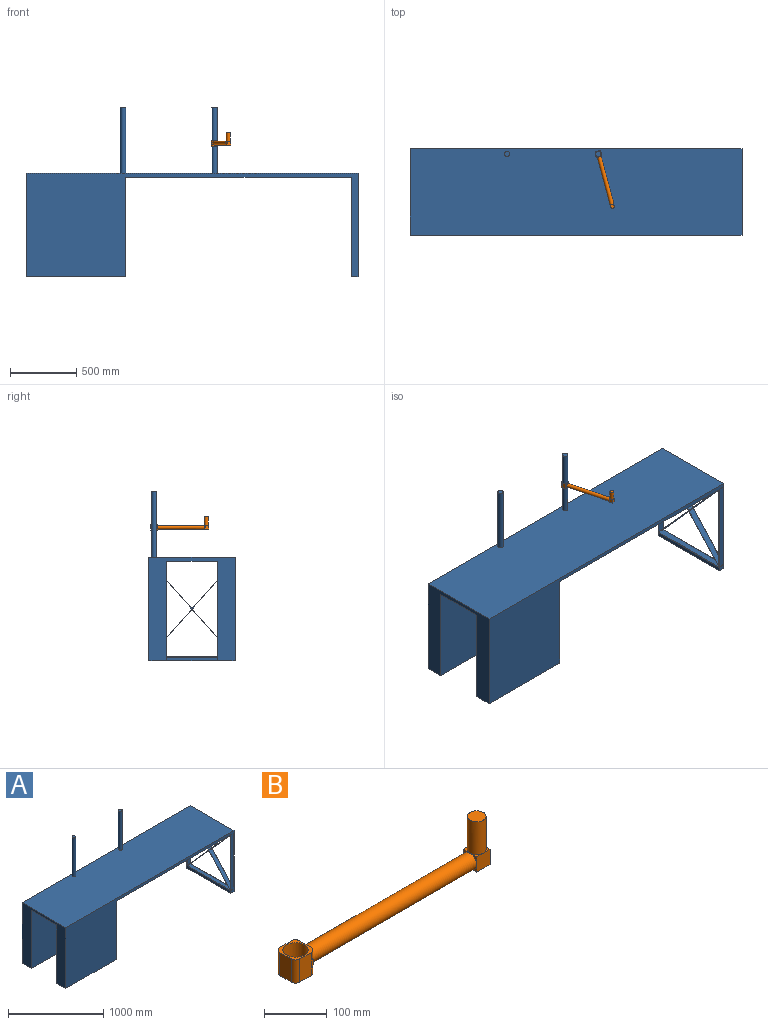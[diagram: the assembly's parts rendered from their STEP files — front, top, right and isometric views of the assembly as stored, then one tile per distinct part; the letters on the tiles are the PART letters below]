
ASSEMBLY  parts=2 mates=1
PART A: 37 faces, bbox 2500x650x1280 mm
  f0: plane 712.61x50mm, normal (0,1,0), area 35630.5mm2, adj f11,f19,f30,f31
  f1: plane 712.61x50mm, normal (0,-1,0), area 35630.5mm2, adj f11,f19,f34,f35
  f2: plane 2500x650mm, normal (0,0,-1), area 1421998.4mm2, adj f8,f9,f10,f11,f13,f14,f16,f17
  f3: plane 638.89x48.8mm, normal (0,0,1), area 31177.8mm2, adj f4,f5,f32,f33
  f4: cylinder r=0.6mm len=639.97mm, axis (0,1,0), area 602.5mm2, adj f3,f19,f32,f33
  f5: cylinder r=0.6mm len=639.97mm, axis (0,-1,0), area 602.5mm2, adj f3,f11,f32,f33
  f6: plane 50x1.1mm, normal (0,1,0), area 25.2mm2, adj f11,f19,f21,f22,f23,f24
  f7: plane 50x1.1mm, normal (0,-1,0), area 25.2mm2, adj f11,f19,f21,f22,f23,f24
  f8: plane 2500x780mm, normal (0,1,0), area 675000mm2, adj f2,f9,f11,f12,f16,f18,f19,f20
  f9: plane 780x650mm, normal (-1,0,0), area 222000mm2, adj f2,f8,f10,f12,f13,f15,f17,f18
  f10: plane 2500x780mm, normal (0,-1,0), area 675000mm2, adj f2,f9,f11,f12,f14,f15,f19,f20
  f11: plane 780x650mm, normal (1,0,0), area 50244.1mm2, adj f0,f1,f2,f5,f6,f7,f8,f10
  f12: plane 2500x650mm, normal (0,0,1), area 1622486.7mm2, adj f8,f9,f10,f11,f25,f27
  f13: plane 750x750mm, normal (0,1,0), area 562500mm2, adj f2,f9,f14,f15
  f14: plane 750x135mm, normal (1,0,0), area 101250mm2, adj f2,f10,f13,f15
  f15: plane 750x135mm, normal (0,0,-1), area 101250mm2, adj f9,f10,f13,f14
  f16: plane 750x135mm, normal (1,0,0), area 101250mm2, adj f2,f8,f17,f18
  f17: plane 750x750mm, normal (0,-1,0), area 562500mm2, adj f2,f9,f16,f18
  f18: plane 750x135mm, normal (0,0,-1), area 101250mm2, adj f8,f9,f16,f17
  f19: plane 750x650mm, normal (-1,0,0), area 30744.1mm2, adj f0,f1,f2,f4,f6,f7,f8,f10
  f20: plane 650x50mm, normal (0,0,-1), area 32500mm2, adj f8,f10,f11,f19
  f21: plane 644x50mm, normal (0,0,1), area 32200mm2, adj f6,f7,f11,f19
  f22: plane 644x48.8mm, normal (0,0,-1), area 31427.2mm2, adj f6,f7,f23,f24
  f23: cylinder r=0.6mm len=644mm, axis (0,1,0), area 607mm2, adj f6,f7,f11,f22
  f24: cylinder r=0.6mm len=644mm, axis (0,-1,0), area 607mm2, adj f6,f7,f19,f22
  f25: cylinder r=20mm len=500mm, axis (0,0,-1), area 62831.9mm2, adj f12,f26
  f26: plane 40x40mm, normal (0,0,1), area 1256.6mm2, adj f25
  f27: cylinder r=20mm len=500mm, axis (0,0,-1), area 62831.9mm2, adj f12,f28
  f28: plane 40x40mm, normal (0,0,1), area 1256.6mm2, adj f27
  f29: plane 356.31x319.98mm, normal (0,0.74,0.67), area 23944.9mm2, adj f2,f11,f19,f36
  f30: plane 356.31x319.98mm, normal (0,-0.74,-0.67), area 23944.9mm2, adj f0,f11,f19,f31
  f31: plane 356.31x319.98mm, normal (0,-0.74,0.67), area 23944.9mm2, adj f0,f11,f19,f30
  f32: plane 356.31x319.98mm, normal (0,0.74,-0.67), area 23904.8mm2, adj f3,f4,f5,f11,f19,f33
  f33: plane 356.31x319.98mm, normal (0,-0.74,-0.67), area 23904.8mm2, adj f3,f4,f5,f11,f19,f32
  f34: plane 356.31x319.98mm, normal (0,0.74,0.67), area 23944.9mm2, adj f1,f11,f19,f35
  f35: plane 356.31x319.98mm, normal (0,0.74,-0.67), area 23944.9mm2, adj f1,f11,f19,f34
  f36: plane 356.31x319.98mm, normal (0,-0.74,0.67), area 23944.9mm2, adj f2,f11,f19,f29
PART B: 31 faces, bbox 445x45x101.5 mm
  f0: plane 25.69x14.75mm, normal (1,0,0), area 247.1mm2, adj f4,f19,f23,f26
  f1: plane 15x15mm, normal (0,0,1), area 48.3mm2, adj f11,f13,f14
  f2: plane 15x15mm, normal (0,0,1), area 48.3mm2, adj f6,f11,f14
  f3: plane 15x15mm, normal (0,0,1), area 48.3mm2, adj f7,f9,f14
  f4: cylinder r=15mm len=370mm, axis (-1,0,0), area 34871.7mm2, adj f0,f5,f6,f7,f8,f21,f24,f27
  f5: plane 15x15mm, normal (-1,0,0), area 48.3mm2, adj f4,f10,f11
  f6: plane 15x15mm, normal (-1,0,0), area 48.3mm2, adj f2,f4,f11
  f7: plane 15x15mm, normal (-1,0,0), area 48.3mm2, adj f3,f4,f9
  f8: plane 15x15mm, normal (-1,0,0), area 48.3mm2, adj f4,f9,f10
  f9: plane 30x30mm, normal (0,-1,0), area 900mm2, adj f3,f7,f8,f10,f12,f13
  f10: plane 30x30mm, normal (0,0,-1), area 900mm2, adj f5,f8,f9,f11,f13
  f11: plane 30x30mm, normal (0,1,0), area 900mm2, adj f1,f2,f5,f6,f10,f13
  f12: plane 15x15mm, normal (0,0,1), area 48.3mm2, adj f9,f13,f14
  f13: plane 30x30mm, normal (1,0,0), area 900mm2, adj f1,f9,f10,f11,f12
  f14: cylinder r=15mm len=64mm, axis (0,0,-1), area 6031.9mm2, adj f1,f2,f3,f12,f15
  f15: plane 30x30mm, normal (0,0,1), area 706.9mm2, adj f14
  f16: plane 45x25.93mm, normal (0,-1,0), area 1157.8mm2, adj f17,f19,f26,f27,f28,f30
  f17: plane 45x45mm, normal (0,0,1), area 688.3mm2, adj f16,f18,f20,f21,f22,f25,f28,f29
  f18: plane 45x25.93mm, normal (0,1,0), area 1157.8mm2, adj f17,f19,f23,f24,f25,f29
  f19: plane 45x45mm, normal (0,0,-1), area 688.3mm2, adj f0,f16,f18,f20,f22,f23,f26,f29
  f20: plane 45x25.69mm, normal (-1,0,0), area 1155.9mm2, adj f17,f19,f29,f30
  f21: plane 25.69x14.75mm, normal (1,0,0), area 247.1mm2, adj f4,f17,f25,f28
  f22: cylinder r=20mm len=45mm, axis (0,0,1), area 5654.9mm2, adj f17,f19
  f23: cylinder r=9.66mm len=14.75mm, axis (0,0,-1), area 223.8mm2, adj f0,f18,f19,f24
  f24: bspline ~15.5x9.66mm, area 212.4mm2, adj f4,f18,f23,f25
  f25: cylinder r=9.66mm len=14.75mm, axis (0,0,-1), area 223.8mm2, adj f17,f18,f21,f24
  f26: cylinder r=9.66mm len=14.75mm, axis (0,0,1), area 223.8mm2, adj f0,f16,f19,f27
  f27: bspline ~15.5x9.66mm, area 212.4mm2, adj f4,f16,f26,f28
  f28: cylinder r=9.66mm len=14.75mm, axis (0,0,1), area 223.8mm2, adj f16,f17,f21,f27
  f29: cylinder r=9.66mm len=45mm, axis (0,0,1), area 682.6mm2, adj f17,f18,f19,f20
  f30: cylinder r=9.66mm len=45mm, axis (0,0,-1), area 682.6mm2, adj f16,f17,f19,f20
PLACE A t=(-374.61,86.69,125.71)mm
PLACE B rot(axis=(0,0,-1),75deg) t=(-184.61,245.72,383.21)mm
MATE cylindrical A.f27 <-> B.f22  axis (0,0,-1) through (-190.44,267.45,405.71)mm
